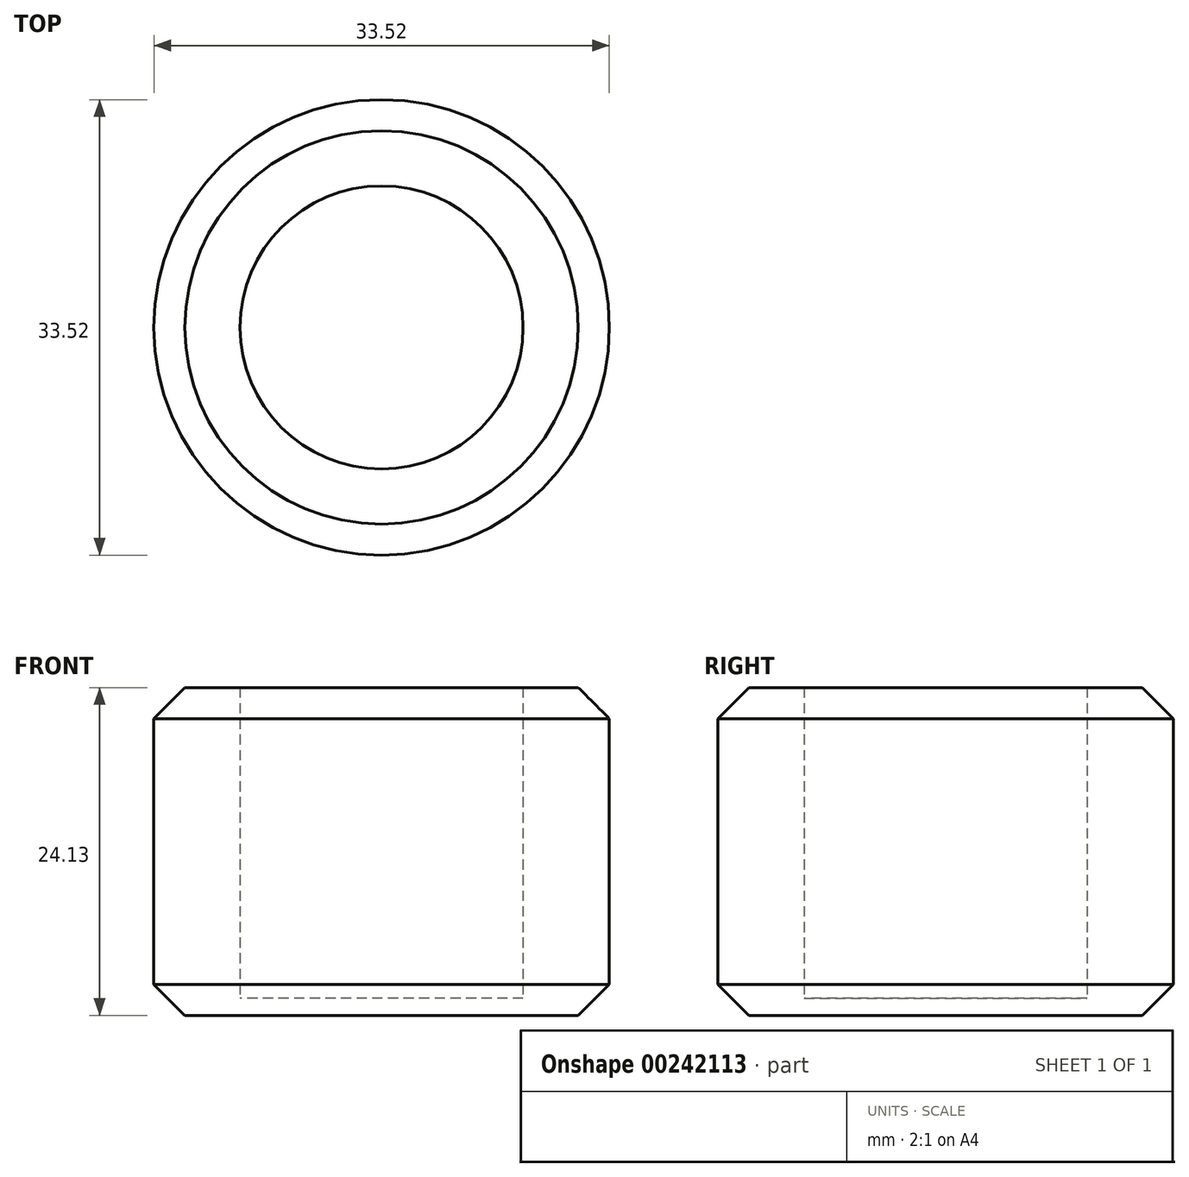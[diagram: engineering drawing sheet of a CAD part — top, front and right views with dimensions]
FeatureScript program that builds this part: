
annotation { "Feature Type Name" : "Feature", "Feature Type Description" : "" }
export const myFeature = defineFeature(function(context is Context, id is Id, definition is map)
    precondition{}
    {
        {
            var Q0;
            Q0=qCreatedBy(makeId("Top.planeOp"),FACE);
            var sketch = newSketch(context, id + "F0", { "sketchPlane" : qUnion([Q0])});
            skCircle(sketch, "E0", {"center": v(0, 0) * mm, "radius": 10.41 * mm});
            skCircle(sketch, "E1.0", {"center": v(0, 0) * mm, "radius": 16.76 * mm});
            skSolve(sketch);
        }
        {
            var Q0;
            Q0=makeQuery(id+"F0.imprint","IMPRINT",FACE,{"disambiguationData":[TD([[makeQuery(id+"F0.imprint","IMPRINT",EDGE,{"derivedFrom":sQuery(id+"F0.wireOp",EDGE,"E0")}),-1.0]])]});
            extrude(context, id + "F1", {"entities" : qUnion([Q0]), "depth" : 22.86 * mm});
        }
        {
            var Q0;
            Q0=makeQuery(id+"F0.imprint","IMPRINT",FACE,{"disambiguationData":[TD([[makeQuery(id+"F0.imprint","IMPRINT",EDGE,{"derivedFrom":sQuery(id+"F0.wireOp",EDGE,"E0")}),-1.0]])]});
            var Q1;
            Q1=makeQuery(id+"F0.imprint","IMPRINT",FACE,{"disambiguationData":[TD([[makeQuery(id+"F0.imprint","IMPRINT",EDGE,{"derivedFrom":sQuery(id+"F0.wireOp",EDGE,"E0")}),1.0]])]});
            extrude(context, id + "F2", {"entities" : qUnion([Q0, Q1]), "operationType" : NewBodyOperationType.ADD, "oppositeDirection" : true, "depth" : 1.27 * mm});
        }
        {
            var Q0;
            Q0=makeQuery(id+"F2.opExtrude","CAP_EDGE",EDGE,{"disambiguationData":[OSD([sQuery(id+"F0.wireOp",EDGE,"E1.0")])],"isStart":false});
            var Q1;
            Q1=makeQuery(id+"F1.opExtrude","CAP_EDGE",EDGE,{"disambiguationData":[OSD([sQuery(id+"F0.wireOp",EDGE,"E1.0")])],"isStart":false});
            chamfer(context, id + "F3", {"entities" : qUnion([Q0, Q1]), "width" : 2.3 * mm, "tangentPropagation" : true});
        }
    });
